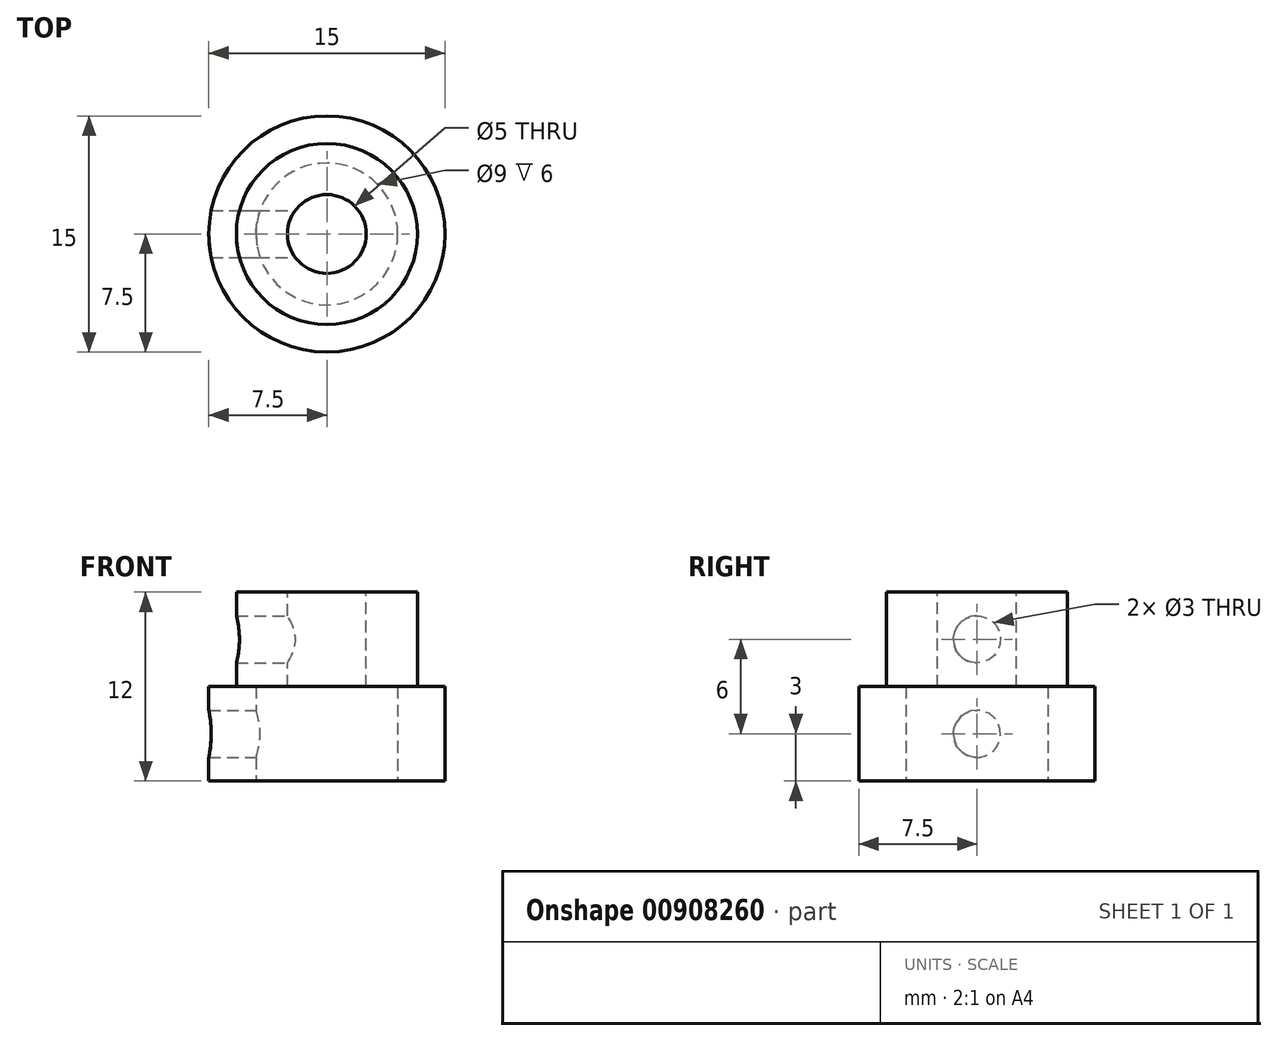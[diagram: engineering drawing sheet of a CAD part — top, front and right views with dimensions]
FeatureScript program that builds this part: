
annotation { "Feature Type Name" : "Feature", "Feature Type Description" : "" }
export const myFeature = defineFeature(function(context is Context, id is Id, definition is map)
    precondition{}
    {
        {
            var Q0;
            Q0=qCreatedBy(makeId("Top.planeOp"),FACE);
            var sketch = newSketch(context, id + "F0", { "sketchPlane" : qUnion([Q0])});
            skCircle(sketch, "E0", {"center": v(0, 0) * mm, "radius": 7.5 * mm});
            skSolve(sketch);
        }
        {
            var Q0;
            Q0 = qSketchRegion(id + "F0", true);
            extrude(context, id + "F1", {"entities" : qUnion([Q0]), "depth" : 6 * mm, "offsetDistance" : 25 * mm});
        }
        {
            var Q0;
            Q0=makeQuery(id+"F1.opExtrude","CAP_FACE",FACE,{"disambiguationData":[OSD([sQuery(id+"F0.wireOp",EDGE,"E0")])],"isStart":false});
            var sketch = newSketch(context, id + "F2", { "sketchPlane" : qUnion([Q0])});
            skCircle(sketch, "E1", {"center": v(0, 0) * mm, "radius": 5.75 * mm});
            skSolve(sketch);
        }
        {
            var Q0;
            Q0 = qSketchRegion(id + "F2", true);
            extrude(context, id + "F3", {"entities" : qUnion([Q0]), "operationType" : NewBodyOperationType.ADD, "depth" : 6 * mm, "offsetDistance" : 25 * mm});
        }
        {
            var Q0;
            Q0=makeQuery(id+"F3.opExtrude","CAP_FACE",FACE,{"disambiguationData":[OSD([sQuery(id+"F2.wireOp",EDGE,"E1")])],"isStart":false});
            var sketch = newSketch(context, id + "F4", { "sketchPlane" : qUnion([Q0])});
            skCircle(sketch, "E2", {"center": v(0, 0) * mm, "radius": 2.5 * mm});
            skSolve(sketch);
        }
        {
            var Q0;
            Q0 = qSketchRegion(id + "F4", true);
            extrude(context, id + "F5", {"entities" : qUnion([Q0]), "operationType" : NewBodyOperationType.REMOVE, "oppositeDirection" : true, "depth" : 6 * mm, "offsetDistance" : 25 * mm});
        }
        {
            var Q0;
            Q0=makeQuery(id+"F1.opExtrude","CAP_FACE",FACE,{"disambiguationData":[OSD([sQuery(id+"F0.wireOp",EDGE,"E0")])],"isStart":true});
            var sketch = newSketch(context, id + "F6", { "sketchPlane" : qUnion([Q0])});
            skCircle(sketch, "E3", {"center": v(0, 0) * mm, "radius": 4.5 * mm});
            skSolve(sketch);
        }
        {
            var Q0;
            Q0 = qSketchRegion(id + "F6", true);
            extrude(context, id + "F7", {"entities" : qUnion([Q0]), "operationType" : NewBodyOperationType.REMOVE, "oppositeDirection" : true, "depth" : 6 * mm, "offsetDistance" : 25 * mm});
        }
        {
            var Q0;
            Q0=qCreatedBy(makeId("Right.planeOp"),FACE);
            var sketch = newSketch(context, id + "F8", { "sketchPlane" : qUnion([Q0])});
            skCircle(sketch, "E4", {"center": v(0, 3) * mm, "radius": 1.5 * mm});
            skCircle(sketch, "E5", {"center": v(0, 9) * mm, "radius": 1.5 * mm});
            skSolve(sketch);
        }
        {
            var Q0;
            Q0 = qSketchRegion(id + "F8", true);
            extrude(context, id + "F9", {"entities" : qUnion([Q0]), "operationType" : NewBodyOperationType.REMOVE, "oppositeDirection" : true, "depth" : 25 * mm, "offsetDistance" : 25 * mm});
        }
    });
